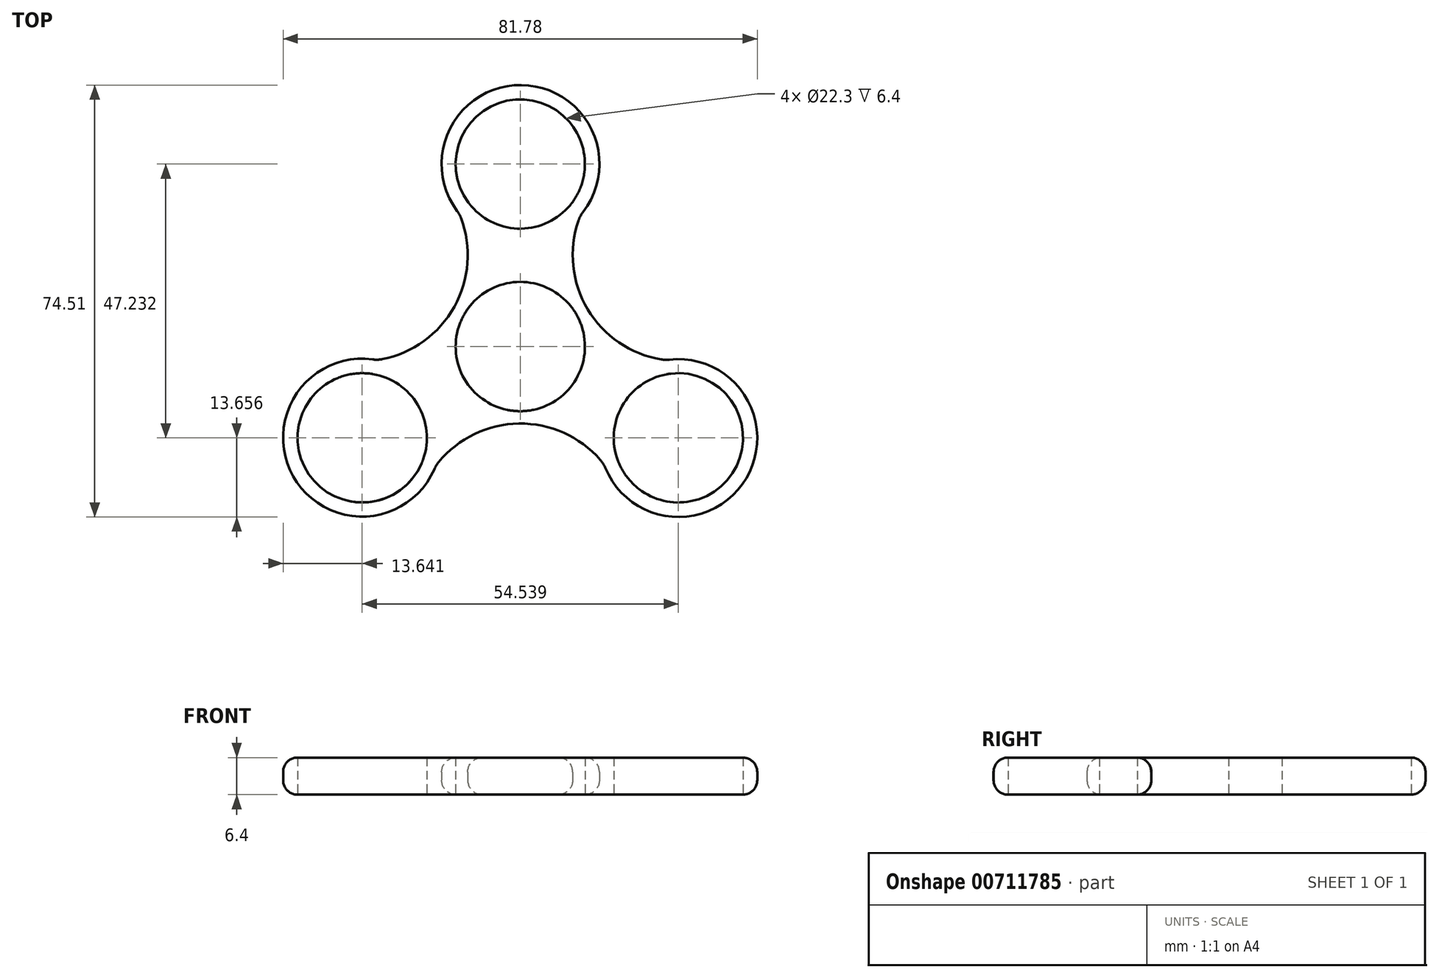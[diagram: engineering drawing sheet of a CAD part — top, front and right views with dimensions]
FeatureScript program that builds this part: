
annotation { "Feature Type Name" : "Feature", "Feature Type Description" : "" }
export const myFeature = defineFeature(function(context is Context, id is Id, definition is map)
    precondition{}
    {
        {
            var Q0;
            Q0=qCreatedBy(makeId("Top.planeOp"),FACE);
            var sketch = newSketch(context, id + "F0", { "sketchPlane" : qUnion([Q0])});
            skCircle(sketch, "E0", {"center": v(0, 0) * mm, "radius": 11.15 * mm});
            skCircle(sketch, "E1", {"center": v(0, 0) * mm, "radius": 12.5 * mm});
            skCircle(sketch, "E2", {"center": v(0, 31.49) * mm, "radius": 11.15 * mm});
            skCircle(sketch, "E3", {"center": v(0, 31.49) * mm, "radius": 12.5 * mm});
            skArc(sketch, "E4", {"start": v(-9.08, 8.6) * mm, "mid": v(-7.31, 16.22) * mm, "end": v(-9.74, 23.66) * mm});
            skArc(sketch, "E5.MirrorCS", {"start": v(9.08, 8.6) * mm, "mid": v(7.31, 16.22) * mm, "end": v(9.74, 23.66) * mm});
            skCircle(sketch, "E6.1.0", {"center": v(-27.27, -15.74) * mm, "radius": 11.15 * mm});
            skArc(sketch, "E6.1.1", {"start": v(-2.9, -12.16) * mm, "mid": v(-10.39, -14.44) * mm, "end": v(-15.62, -20.27) * mm});
            skArc(sketch, "E6.1.2", {"start": v(-11.98, 3.56) * mm, "mid": v(-17.7, -1.78) * mm, "end": v(-25.36, -3.4) * mm});
            skCircle(sketch, "E6.1.3", {"center": v(-27.27, -15.74) * mm, "radius": 12.5 * mm});
            skCircle(sketch, "E6.2.0", {"center": v(27.27, -15.74) * mm, "radius": 11.15 * mm});
            skArc(sketch, "E6.2.1", {"start": v(11.98, 3.56) * mm, "mid": v(17.7, -1.78) * mm, "end": v(25.36, -3.4) * mm});
            skArc(sketch, "E6.2.2", {"start": v(2.9, -12.16) * mm, "mid": v(10.39, -14.44) * mm, "end": v(15.62, -20.27) * mm});
            skCircle(sketch, "E6.2.3", {"center": v(27.27, -15.74) * mm, "radius": 12.5 * mm});
            skArc(sketch, "E7", {"start": v(10.8, 23.17) * mm, "mid": v(0.18, 45.11) * mm, "end": v(-10.9, 23.4) * mm});
            skArc(sketch, "E8.1.0", {"start": v(-25.47, -2.23) * mm, "mid": v(-39.16, -22.4) * mm, "end": v(-14.82, -21.14) * mm});
            skArc(sketch, "E8.2.0", {"start": v(14.66, -20.94) * mm, "mid": v(38.97, -22.72) * mm, "end": v(25.72, -2.26) * mm});
            skArc(sketch, "E9", {"start": v(10.03, 21.73) * mm, "mid": v(11.63, 6.44) * mm, "end": v(24.33, -2.23) * mm});
            skArc(sketch, "E10.1.0", {"start": v(-23.84, -2.18) * mm, "mid": v(-11.39, 6.85) * mm, "end": v(-10.24, 22.18) * mm});
            skArc(sketch, "E10.2.0", {"start": v(13.8, -19.55) * mm, "mid": v(-0.24, -13.29) * mm, "end": v(-14.1, -19.96) * mm});
            skPoint(sketch, "E11.visualSharp", {"position": v(-24.78, -2.34) * mm});
            skArc(sketch, "E11.filletArc", {"start": v(-25.47, -2.23) * mm, "mid": v(-24.65, -2.27) * mm, "end": v(-23.84, -2.18) * mm});
            skPoint(sketch, "E12.visualSharp", {"position": v(-14.6, -20.6) * mm});
            skArc(sketch, "E12.filletArc", {"start": v(-14.1, -19.96) * mm, "mid": v(-14.5, -20.52) * mm, "end": v(-14.82, -21.14) * mm});
            skPoint(sketch, "E13.visualSharp", {"position": v(14.42, -20.3) * mm});
            skArc(sketch, "E13.filletArc", {"start": v(14.66, -20.94) * mm, "mid": v(14.3, -20.21) * mm, "end": v(13.8, -19.55) * mm});
            skPoint(sketch, "E14.visualSharp", {"position": v(25.13, -2.34) * mm});
            skArc(sketch, "E14.filletArc", {"start": v(24.33, -2.23) * mm, "mid": v(25.02, -2.3) * mm, "end": v(25.72, -2.26) * mm});
            skPoint(sketch, "E15.visualSharp", {"position": v(10.36, 22.63) * mm});
            skArc(sketch, "E15.filletArc", {"start": v(10.8, 23.17) * mm, "mid": v(10.36, 22.48) * mm, "end": v(10.03, 21.73) * mm});
            skPoint(sketch, "E16.visualSharp", {"position": v(-10.54, 22.94) * mm});
            skArc(sketch, "E16.filletArc", {"start": v(-10.24, 22.18) * mm, "mid": v(-10.53, 22.82) * mm, "end": v(-10.9, 23.4) * mm});
            skCircle(sketch, "E17", {"center": v(0, 0) * mm, "radius": 45.35 * mm, "construction": true});
            skSolve(sketch);
        }
        {
            var Q0;
            Q0=makeQuery(id+"F0.imprint","IMPRINT",FACE,{"disambiguationData":[TD([[makeQuery(id+"F0.imprint","IMPRINT",EDGE,{"derivedFrom":sQuery(id+"F0.wireOp",EDGE,"E2")}),-1.0]])]});
            var Q1;
            {var subQ0=sQuery(id+"F0.wireOp",EDGE,"E4");Q1=makeQuery(id+"F0.imprint","IMPRINT",FACE,{"disambiguationData":[TD([[makeQuery(id+"F0.imprint","IMPRINT",EDGE,{"derivedFrom":subQ0}),-1.0]])]});}
            var Q2;
            {var subQ0=sQuery(id+"F0.wireOp",EDGE,"E6.1.1");Q2=makeQuery(id+"F0.imprint","IMPRINT",FACE,{"disambiguationData":[TD([[makeQuery(id+"F0.imprint","IMPRINT",EDGE,{"derivedFrom":subQ0}),-1.0]])]});}
            var Q3;
            Q3=makeQuery(id+"F0.imprint","IMPRINT",FACE,{"disambiguationData":[TD([[makeQuery(id+"F0.imprint","IMPRINT",EDGE,{"derivedFrom":sQuery(id+"F0.wireOp",EDGE,"E6.1.0")}),-1.0]])]});
            var Q4;
            Q4=makeQuery(id+"F0.imprint","IMPRINT",FACE,{"disambiguationData":[TD([[makeQuery(id+"F0.imprint","IMPRINT",EDGE,{"derivedFrom":sQuery(id+"F0.wireOp",EDGE,"E0")}),-1.0]])]});
            var Q5;
            {var subQ0=sQuery(id+"F0.wireOp",EDGE,"E6.2.1");Q5=makeQuery(id+"F0.imprint","IMPRINT",FACE,{"disambiguationData":[TD([[makeQuery(id+"F0.imprint","IMPRINT",EDGE,{"derivedFrom":subQ0}),-1.0]])]});}
            var Q6;
            Q6=makeQuery(id+"F0.imprint","IMPRINT",FACE,{"disambiguationData":[TD([[makeQuery(id+"F0.imprint","IMPRINT",EDGE,{"derivedFrom":sQuery(id+"F0.wireOp",EDGE,"E6.2.0")}),-1.0]])]});
            var Q7;
            {var subQ3=sQuery(id+"F0.wireOp",EDGE,"E4");Q7=makeQuery(id+"F0.imprint","IMPRINT",FACE,{"disambiguationData":[TD([[makeQuery(id+"F0.imprint","IMPRINT",EDGE,{"derivedFrom":subQ3}),1.0]])]});}
            extrude(context, id + "F1", {"entities" : qUnion([Q0, Q1, Q2, Q3, Q4, Q5, Q6, Q7]), "depth" : 6.4 * mm, "offsetDistance" : 25 * mm});
        }
        {
            var Q0;
            Q0=makeQuery(id+"F1.opExtrude","SWEPT_FACE",FACE,{"disambiguationData":[OSD([sQuery(id+"F0.wireOp",EDGE,"E8.1.0")])]});
            var Q1;
            Q1=makeQuery(id+"F1.opExtrude","SWEPT_FACE",FACE,{"disambiguationData":[OSD([sQuery(id+"F0.wireOp",EDGE,"E10.2.0")])]});
            var Q2;
            Q2=makeQuery(id+"F1.opExtrude","SWEPT_FACE",FACE,{"disambiguationData":[OSD([sQuery(id+"F0.wireOp",EDGE,"E12.filletArc")])]});
            var Q3;
            Q3=makeQuery(id+"F1.opExtrude","SWEPT_FACE",FACE,{"disambiguationData":[OSD([sQuery(id+"F0.wireOp",EDGE,"E8.2.0")])]});
            var Q4;
            Q4=makeQuery(id+"F1.opExtrude","SWEPT_FACE",FACE,{"disambiguationData":[OSD([sQuery(id+"F0.wireOp",EDGE,"E9")])]});
            var Q5;
            Q5=makeQuery(id+"F1.opExtrude","SWEPT_FACE",FACE,{"disambiguationData":[OSD([sQuery(id+"F0.wireOp",EDGE,"E7")])]});
            var Q6;
            Q6=makeQuery(id+"F1.opExtrude","SWEPT_FACE",FACE,{"disambiguationData":[OSD([sQuery(id+"F0.wireOp",EDGE,"E10.1.0")])]});
            var Q7;
            Q7=makeQuery(id+"F1.opExtrude","SWEPT_FACE",FACE,{"disambiguationData":[OSD([sQuery(id+"F0.wireOp",EDGE,"E11.filletArc")])]});
            var Q8;
            Q8=makeQuery(id+"F1.opExtrude","SWEPT_FACE",FACE,{"disambiguationData":[OSD([sQuery(id+"F0.wireOp",EDGE,"E16.filletArc")])]});
            var Q9;
            Q9=makeQuery(id+"F1.opExtrude","SWEPT_FACE",FACE,{"disambiguationData":[OSD([sQuery(id+"F0.wireOp",EDGE,"E13.filletArc")])]});
            var Q10;
            Q10=makeQuery(id+"F1.opExtrude","SWEPT_FACE",FACE,{"disambiguationData":[OSD([sQuery(id+"F0.wireOp",EDGE,"E14.filletArc")])]});
            var Q11;
            Q11=makeQuery(id+"F1.opExtrude","SWEPT_FACE",FACE,{"disambiguationData":[OSD([sQuery(id+"F0.wireOp",EDGE,"E15.filletArc")])]});
            fillet(context, id + "F2", {"entities" : qUnion([Q0, Q1, Q2, Q3, Q4, Q5, Q6, Q7, Q8, Q9, Q10, Q11]), "radius" : 2.5 * mm, "tangentPropagation" : true, "allowEdgeOverflow" : false});
        }
    });
